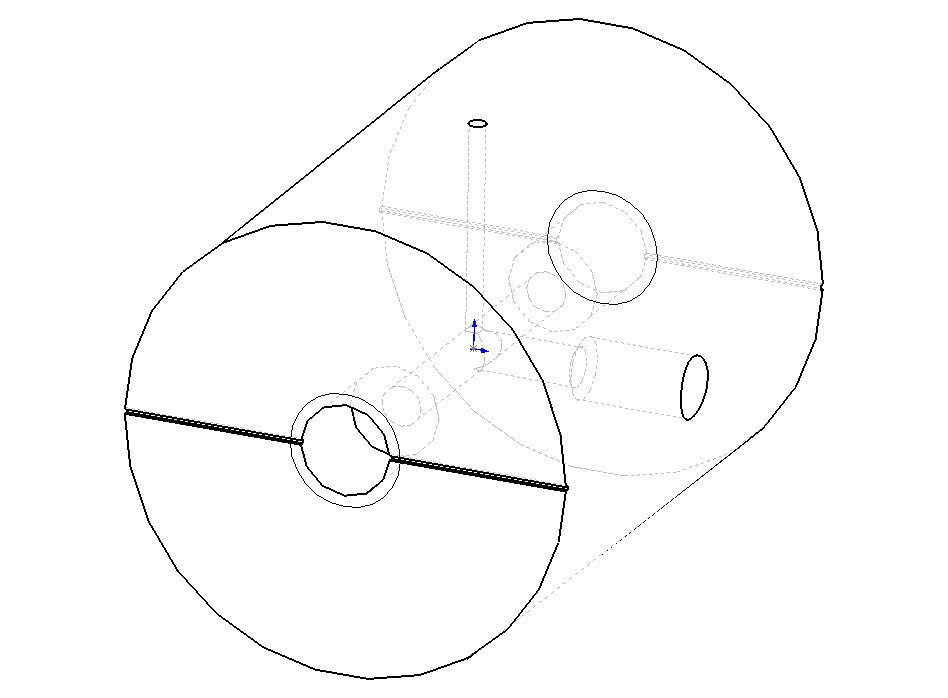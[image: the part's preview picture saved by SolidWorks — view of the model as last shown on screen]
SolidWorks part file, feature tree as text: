
SOLIDWORKS PART (.sldprt)
format: sldprt  version: not decoded by parser v0  size: 514,560 bytes
history: native  units: mm
features: sketch x9, cut_extrude x4, hole x2, mirror x2, material x1, extrude x1, thread x1, plane x1 (+12 scaffold rows collapsed)
feature tree (33):
  scaffold x12  (default folders/planes/origin — collapsed)
  material  "Material <not specified>"
  sketch  "Sketch1"  dims[D1=25.4mm]
  extrude  "Base-Extrude"  Depth=33mm
  hole  "1/4-20 Tapped Hole1"  [1 undecoded]
  sketch  "Sketch3"
  thread  "Cosmetic Thread1"  Diameter=6.35mm  [1 undecoded]
  sketch  "Sketch2"  dims[hole-wizard template sketch: 47 standard entries collapsed; hole parameters kept: c15.Tap Drill Depth=6.35mm c15.D3=~14.816244mm c15.Drill Angle=118.0deg]
  mirror  "Mirror1"
  sketch  "Sketch4"  dims[D1=2.2606mm]
  cut_extrude  "Cut-Extrude1"  [1 undecoded]
  plane  "Plane1"  Offset=12.7mm
  hole  "#8-32 Tapped Hole1"  Diameter=3.4544mm Depth=6.35mm
  sketch  "Sketch8"
  sketch  "Sketch7"  dims[hole-wizard template sketch: 47 standard entries collapsed; hole parameters kept: c15.Tap Drill Depth=6.35mm c15.D3=~14.816244mm c15.Drill Angle=118.0deg]
  sketch  "Sketch9"  dims[D1=2.2606mm]
  cut_extrude  "Cut-Extrude2"  [1 undecoded]
  sketch  "Sketch10"  dims[D1=0.25mm]
  cut_extrude  "Cut-Extrude3"  Depth=0.25mm
  mirror  "Mirror2"
  sketch  "Sketch11"  dims[D1=1.0mm]
  cut_extrude  "Cut-Extrude4"  [1 undecoded]
decode coverage: 11 of 19 modeling features carry decoded parameters
note: ~ marks probable driven/reference dimensions
note: 5 parameter values undecoded
summary: no parameter record found for 4 features
note: suppression state not decoded; provenance and decode notes live in map.json
